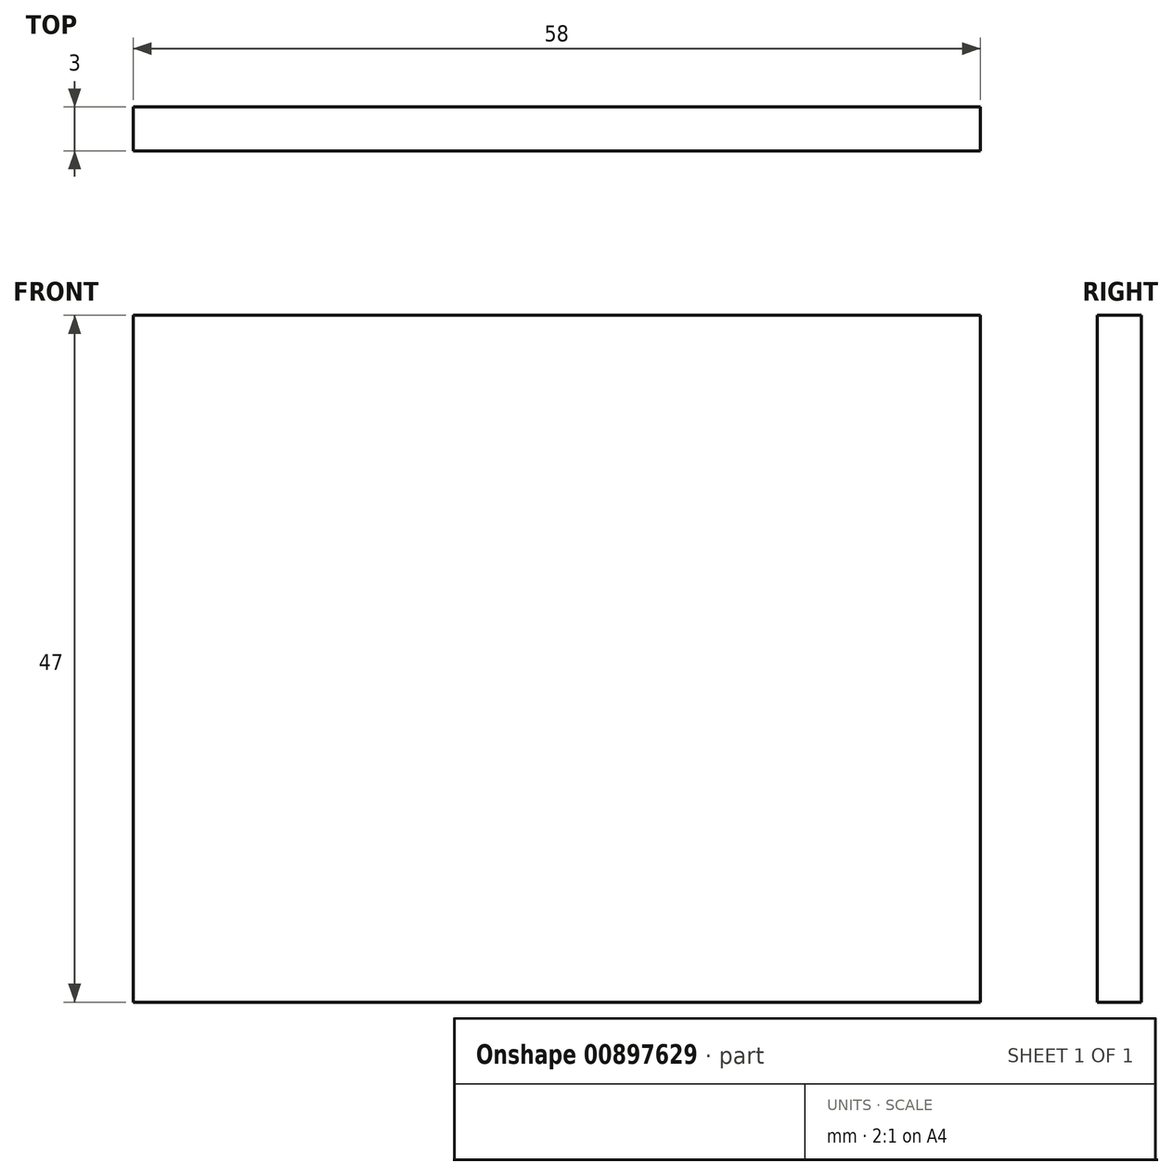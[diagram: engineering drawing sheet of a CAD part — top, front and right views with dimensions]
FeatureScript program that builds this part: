
annotation { "Feature Type Name" : "Feature", "Feature Type Description" : "" }
export const myFeature = defineFeature(function(context is Context, id is Id, definition is map)
    precondition{}
    {
        {
            var Q0;
            Q0=qCreatedBy(makeId("Front.planeOp"),FACE);
            var sketch = newSketch(context, id + "F0", { "sketchPlane" : qUnion([Q0])});
            skLineSegment(sketch, "E0.bottom", {"start": v(29, 23.5) * mm, "end": v(-29, 23.5) * mm});
            skLineSegment(sketch, "E0.top", {"start": v(29, -23.5) * mm, "end": v(-29, -23.5) * mm});
            skLineSegment(sketch, "E0.left", {"start": v(29, 23.5) * mm, "end": v(29, -23.5) * mm});
            skLineSegment(sketch, "E0.right", {"start": v(-29, 23.5) * mm, "end": v(-29, -23.5) * mm});
            skPoint(sketch, "E0.middle", {"position": v(0, 0) * mm});
            skSolve(sketch);
        }
        {
            var Q0;
            Q0=makeQuery(id+"F0.imprint","IMPRINT",FACE,{"disambiguationData":[TD([[makeQuery(id+"F0.imprint","IMPRINT",EDGE,{"derivedFrom":sQuery(id+"F0.wireOp",EDGE,"E0.bottom")}),1.0]])]});
            extrude(context, id + "F1", {"entities" : qUnion([Q0]), "depth" : 3 * mm, "offsetDistance" : 25 * mm});
        }
    });
